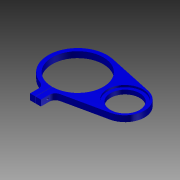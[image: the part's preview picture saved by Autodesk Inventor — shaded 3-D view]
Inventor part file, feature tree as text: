
AUTODESK INVENTOR PART (.ipt)
format: ipt  version: 2012 SP1 (Build 160190100, 190)  size: 150,528 bytes
history: native  units: in
note: dims shown in document units (in); Inventor stores cm internally (conversion verified against a paired STEP export)
features: sketch x5, extrude x3, hole x2, fillet x1
ambient origin geometry x8: Origin, YZ Plane, XZ Plane, XY Plane, X Axis, Y Axis, Z Axis, Center Point
bodies: Solid1 (feature_tree)
feature tree (11):
  extrude  "Extrusion1"  Depth=2.3957in
  hole  "Hole1"  [1 undecoded]
  extrude  "Extrusion2"  Depth=1.695in
  extrude  "Extrusion3"  Depth=1.1811in
  hole  "Hole2"  [1 undecoded]
  fillet  "Fillet1"  Radius=0.2402in
  sketch  "Sketch2"  dims[d1=2.05in d2=2.3957in]
  sketch  "Sketch3"  dims[d3=1.415in d4=1.561in]
  sketch  "Sketch4"  dims[d6=0.2402in d7=0.0in d8=1.695in]
  sketch  "Sketch5"  dims[d9=0.4331in d10=1.1811in]
  sketch  "Sketch6"  dims[d11=1.1811in d12=0.275in d13=0.2402in d14=0.1201in d15=0.085in d16=0.207in d17=0.1575in d18=0.0787in d19=90.0deg d20=0.207in d21=0.0in d22=1.1693in d23=0.165in d24=0.0in d25=0.0197in d26=0.3937in d27=0.0in d28=0.116in d29=0.75in d30=0.25in d31=0.125in d32=0.5635in d33=1.0in d34=0.0in d35=0.25in d36=1.8967in]
note: 2 required parameter values undecoded (feature->parameter linkage not recoverable at this tier; creation-order binding heuristic only, values carry confidence <= 0.55)
